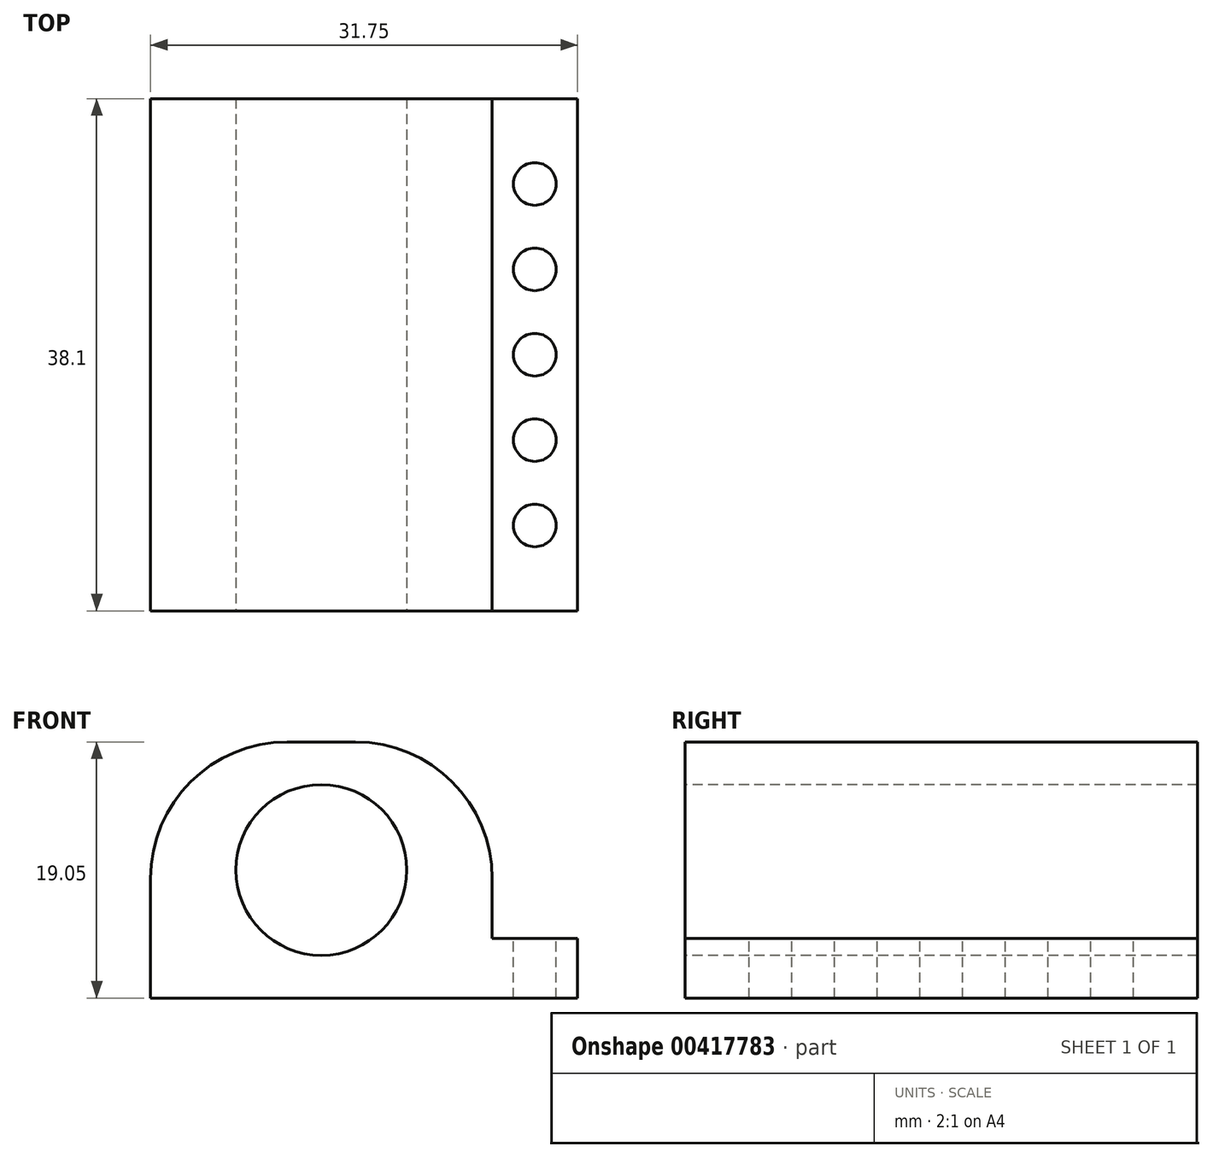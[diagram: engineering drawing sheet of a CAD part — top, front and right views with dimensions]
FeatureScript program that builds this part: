
annotation { "Feature Type Name" : "Feature", "Feature Type Description" : "" }
export const myFeature = defineFeature(function(context is Context, id is Id, definition is map)
    precondition{}
    {
        {
            var Q0;
            Q0=qCreatedBy(makeId("Top.planeOp"),FACE);
            var sketch = newSketch(context, id + "F0", { "sketchPlane" : qUnion([Q0])});
            skLineSegment(sketch, "E0.bottom", {"start": v(0, 0) * mm, "end": v(25.4, 0) * mm});
            skLineSegment(sketch, "E0.top", {"start": v(0, 38.1) * mm, "end": v(25.4, 38.1) * mm});
            skLineSegment(sketch, "E0.left", {"start": v(0, 0) * mm, "end": v(0, 38.1) * mm});
            skLineSegment(sketch, "E0.right", {"start": v(25.4, 0) * mm, "end": v(25.4, 38.1) * mm});
            skSolve(sketch);
        }
        {
            var Q0;
            Q0=makeQuery(id+"F0.imprint","IMPRINT",FACE,{"disambiguationData":[TD([[makeQuery(id+"F0.imprint","IMPRINT",EDGE,{"derivedFrom":sQuery(id+"F0.wireOp",EDGE,"E0.bottom")}),1.0]])]});
            extrude(context, id + "F1", {"entities" : qUnion([Q0]), "depth" : 19.05 * mm});
        }
        {
            var Q0;
            Q0=makeQuery(id+"F1.opExtrude","SWEPT_FACE",FACE,{"disambiguationData":[OSD([sQuery(id+"F0.wireOp",EDGE,"E0.bottom")])]});
            var sketch = newSketch(context, id + "F2", { "sketchPlane" : qUnion([Q0])});
            skLineSegment(sketch, "E1", {"start": v(12.7, 0) * mm, "end": v(12.7, 9.53) * mm});
            skPoint(sketch, "E1.endSnap0", {"position": v(12.7, 19.05) * mm});
            skCircle(sketch, "E2", {"center": v(12.7, 9.53) * mm, "radius": 6.35 * mm});
            skSolve(sketch);
        }
        {
            var Q0;
            Q0=makeQuery(id+"F2.imprint","IMPRINT",FACE,{"disambiguationData":[TD([[makeQuery(id+"F2.imprint","IMPRINT",EDGE,{"derivedFrom":sQuery(id+"F2.wireOp",EDGE,"E2")}),1.0]])]});
            var Q1;
            Q1=makeQuery(id+"F1.opExtrude","SWEPT_FACE",FACE,{"disambiguationData":[OSD([sQuery(id+"F0.wireOp",EDGE,"E0.top")])]});
            extrude(context, id + "F3", {"entities" : qUnion([Q0]), "operationType" : NewBodyOperationType.REMOVE, "endBound" : BoundingType.UP_TO_SURFACE, "oppositeDirection" : true, "endBoundEntityFace" : qUnion([Q1]), "depth" : 25.4 * mm});
        }
        {
            var Q0;
            Q0=makeQuery(id+"F1.opExtrude","CAP_EDGE",EDGE,{"disambiguationData":[OSD([sQuery(id+"F0.wireOp",EDGE,"E0.right")])],"isStart":false});
            var Q1;
            Q1=makeQuery(id+"F1.opExtrude","CAP_EDGE",EDGE,{"disambiguationData":[OSD([sQuery(id+"F0.wireOp",EDGE,"E0.left")])],"isStart":false});
            fillet(context, id + "F4", {"entities" : qUnion([Q0, Q1]), "radius" : 10.16 * mm, "tangentPropagation" : true, "allowEdgeOverflow" : false});
        }
        {
            var Q0;
            Q0=makeQuery(id+"F1.opExtrude","SWEPT_FACE",FACE,{"disambiguationData":[OSD([sQuery(id+"F0.wireOp",EDGE,"E0.right")])]});
            var sketch = newSketch(context, id + "F5", { "sketchPlane" : qUnion([Q0])});
            skLineSegment(sketch, "E3.bottom", {"start": v(0, 0) * mm, "end": v(38.1, 0) * mm});
            skLineSegment(sketch, "E3.top", {"start": v(0, 4.45) * mm, "end": v(38.1, 4.45) * mm});
            skLineSegment(sketch, "E3.left", {"start": v(0, 0) * mm, "end": v(0, 4.45) * mm});
            skLineSegment(sketch, "E3.right", {"start": v(38.1, 0) * mm, "end": v(38.1, 4.45) * mm});
            skSolve(sketch);
        }
        {
            var Q0;
            Q0 = qSketchRegion(id + "F5", true);
            extrude(context, id + "F6", {"entities" : qUnion([Q0]), "operationType" : NewBodyOperationType.ADD, "depth" : 6.35 * mm});
        }
        {
            var Q0;
            Q0=qCreatedBy(makeId("Right.planeOp"),FACE);
            cPlane(context, id + "F7", {"entities" : qUnion([Q0]), "cplaneType" : CPlaneType.OFFSET, "offset" : 12.7 * mm, "width" : 152.4 * mm, "height" : 152.4 * mm});
        }
        {
            var Q0;
            Q0=makeQuery(id+"F6.opExtrude","SWEPT_FACE",FACE,{"disambiguationData":[OSD([sQuery(id+"F5.wireOp",EDGE,"E3.top")])]});
            var sketch = newSketch(context, id + "F8", { "sketchPlane" : qUnion([Q0])});
            skLineSegment(sketch, "E4", {"start": v(28.58, 0) * mm, "end": v(28.57, 38.1) * mm});
            skPoint(sketch, "E5", {"position": v(28.57, 31.75) * mm});
            skPoint(sketch, "E6", {"position": v(28.58, 6.35) * mm});
            skPoint(sketch, "E7", {"position": v(28.58, 12.7) * mm});
            skPoint(sketch, "E8", {"position": v(28.57, 25.4) * mm});
            skPoint(sketch, "E9", {"position": v(28.57, 19.05) * mm});
            skSolve(sketch);
        }
        {
            var Q0;
            Q0=sQuery(id+"F8.wireOp",VERTEX,"E6");
            var Q1;
            Q1=sQuery(id+"F8.wireOp",VERTEX,"E7");
            var Q2;
            Q2=sQuery(id+"F8.wireOp",VERTEX,"E9");
            var Q3;
            Q3=sQuery(id+"F8.wireOp",VERTEX,"E8");
            var Q4;
            Q4=sQuery(id+"F8.wireOp",VERTEX,"E5");
            var Q5;
            Q5=makeQuery(id+"F1.opExtrude","SWEPT_BODY",BODY,{"disambiguationData":[OSD([sQuery(id+"F0.wireOp",EDGE,"E0.bottom"),sQuery(id+"F0.wireOp",EDGE,"E0.top"),sQuery(id+"F0.wireOp",EDGE,"E0.left"),sQuery(id+"F0.wireOp",EDGE,"E0.right")])]});
            hole(context, id + "F9", {"style" : HoleStyle.SIMPLE, "endStyle" : HoleEndStyle.THROUGH, "holeDiameter" : 3.17 * mm, "isTappedThrough" : true, "tappedDepth" : 12.7 * mm, "tapClearance" : 3, "locations" : qUnion([Q0, Q1, Q2, Q3, Q4]), "scope" : qUnion([Q5])});
        }
    });
